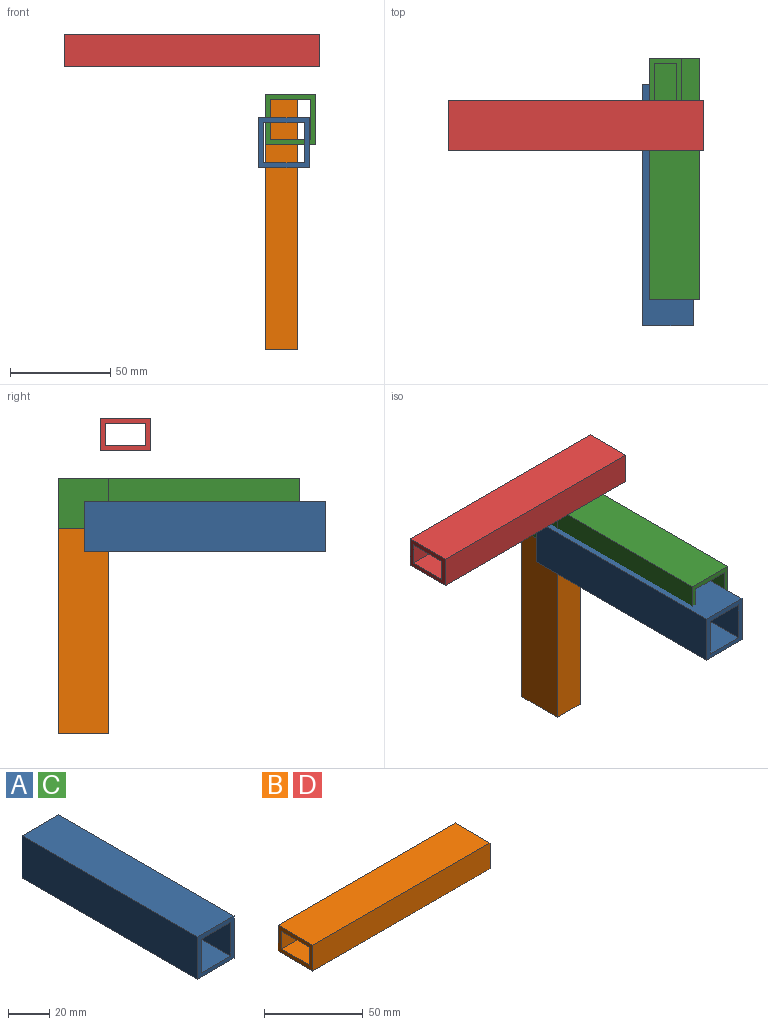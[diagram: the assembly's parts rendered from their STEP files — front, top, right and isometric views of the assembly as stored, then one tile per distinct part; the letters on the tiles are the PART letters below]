
ASSEMBLY  parts=4 mates=1
PART A: 10 faces, bbox 25x120x25 mm
  f0: plane 25x25mm, normal (0,-1,0), area 225mm2, adj f2,f3,f4,f5,f6,f7,f8,f9
  f1: plane 25x25mm, normal (0,1,0), area 225mm2, adj f2,f3,f4,f5,f6,f7,f8,f9
  f2: plane 120x25mm, normal (0,0,-1), area 3000mm2, adj f0,f1,f4,f5
  f3: plane 120x25mm, normal (0,0,1), area 3000mm2, adj f0,f1,f4,f5
  f4: plane 120x25mm, normal (1,0,0), area 3000mm2, adj f0,f1,f2,f3
  f5: plane 120x25mm, normal (-1,0,0), area 3000mm2, adj f0,f1,f2,f3
  f6: plane 120x20mm, normal (0,0,1), area 2400mm2, adj f0,f1,f8,f9
  f7: plane 120x20mm, normal (0,0,-1), area 2400mm2, adj f0,f1,f8,f9
  f8: plane 120x20mm, normal (-1,0,0), area 2400mm2, adj f0,f1,f6,f7
  f9: plane 120x20mm, normal (1,0,0), area 2400mm2, adj f0,f1,f6,f7
PART B: 10 faces, bbox 127x25x16 mm
  f0: plane 25x16mm, normal (-1,0,0), area 180mm2, adj f2,f3,f4,f5,f6,f7,f8,f9
  f1: plane 25x16mm, normal (1,0,0), area 180mm2, adj f2,f3,f4,f5,f6,f7,f8,f9
  f2: plane 127x25mm, normal (0,0,-1), area 3175mm2, adj f0,f1,f4,f5
  f3: plane 127x25mm, normal (0,0,1), area 3175mm2, adj f0,f1,f4,f5
  f4: plane 127x16mm, normal (0,-1,0), area 2032mm2, adj f0,f1,f2,f3
  f5: plane 127x16mm, normal (0,1,0), area 2032mm2, adj f0,f1,f2,f3
  f6: plane 127x20mm, normal (0,0,1), area 2540mm2, adj f0,f1,f8,f9
  f7: plane 127x20mm, normal (0,0,-1), area 2540mm2, adj f0,f1,f8,f9
  f8: plane 127x11mm, normal (0,1,0), area 1397mm2, adj f0,f1,f6,f7
  f9: plane 127x11mm, normal (0,-1,0), area 1397mm2, adj f0,f1,f6,f7
PART C: same geometry as A
PART D: same geometry as B
PLACE A t=(14.9,-13.05,-11.63)mm
PLACE B rot(axis=(0,-1,0),90deg) t=(59.23,58.86,-26.5)mm
PLACE C t=(17.99,0,0)mm
PLACE D t=(4.39,37.77,2.76)mm
MATE fastened B.f1 <-> C.f3  axis (0,0,-1) through (17.99,58.86,14.21)mm
